# Revit family: Sensor-Lutron-Radio_Powr_Savr_Daylight
name_source: partatom
category: Lighting Devices
revit_build: Autodesk Revit 2017 (Build: 20160720_1515(x64)
units: mm (PartAtom-declared; Revit-internal decimal feet)

## family parameters
Cut with Voids When Loaded = No
Host = Face
Maintain Annotation Orientation = No
OmniClass Number = 23.85.80.11.27
OmniClass Title = Lighting Controls
Part Type = Normal
Room Calculation Point = No
Round Connector Dimension = Use Diameter
Shared = No

## types (1)
- LRF2-DCRB-WH
    Arrow Light Horizontal Offset = 0' - 0"
    Arrow Light Tip Depth Offset = 0' - 0"
    Arrow Vertical Offset = 0' - 0"
    Arrow Void Depth = 0' - 0 1/2"
    Arrow Void Height = 0' - 0"
    Arrow Void Horizontal Offset = 0' - 0"
    Arrow Void Tip Depth Offset = 0' - 0"
    Assembly Code = D5030800
    Bottom Cover Radius = 0' - 2 1/2"
    Button Height = 0' - 0"
    Button Vertical Offset = 0' - 0"
    Center Button Depth Offset = 0' - 0 1/2"
    Cost = 0 $
    Cover Angle = 165.00°
    Cover Height = 0' - 0"
    Current = 0 A
    Default Elevation = 0' - 0"
    Description = Wireless Daylight Sensor
    Electrical Potential = 3 V
    Frequency and Channel Codes = 431.0 – 437.0 MHz (U.S.A.; Canada; Mexico; Brazil)
    Instruction Sheet Link = http://www.lutron.com
    Label = DS
    Light Range = 150 fc
    Manufacturer = Lutron Electronics Co., Inc
    Manufacturer Fax Number = 610-282-1243
    Maximum Operating Temperature = 104 °F
    Minimum Operating Temperature = 32 °F
    Model = LRF2-DCRB-WH
    Overall Depth = 0' - 1 1/2"
    Overall Height = 0' - 0 1/2"
    Overall Width = 0' - 1 1/2"
    Performance URL = http://www.lutron.com
    Product Documentation Link = http://www.lutron.com
    Product Name = Wireless Daylight Sensor
    Product Page URL = http://www.lutron.com
    Range = 30' - 0"
    Range End Angle = 172.50°
    Range Start Angle = 7.50°
    Sensor Bottom Body Height = 0' - 0 1/2"
    Sensor Cover Angle = 195.00°
    Sensor Material = Plastic - Lutron - White
    Sensor Radius = 0' - 1"
    Sensor Top Body Height = 0' - 0 1/2"
    Series = Radio Powr Savr
    Side Buttons Depth Offset = 0' - 0"
    Side Buttons Horizontal Offset = 0' - 0 1/2"
    URL = http://www.lutron.com
    Version = 2017 - v1.0b
    Video Link = https://www.youtube.com
    Warranty URL = http://www.lutron.com

## geometry (parser evidence)
native form markers: Sweep x4
no freeform markers — native parametric forms only
